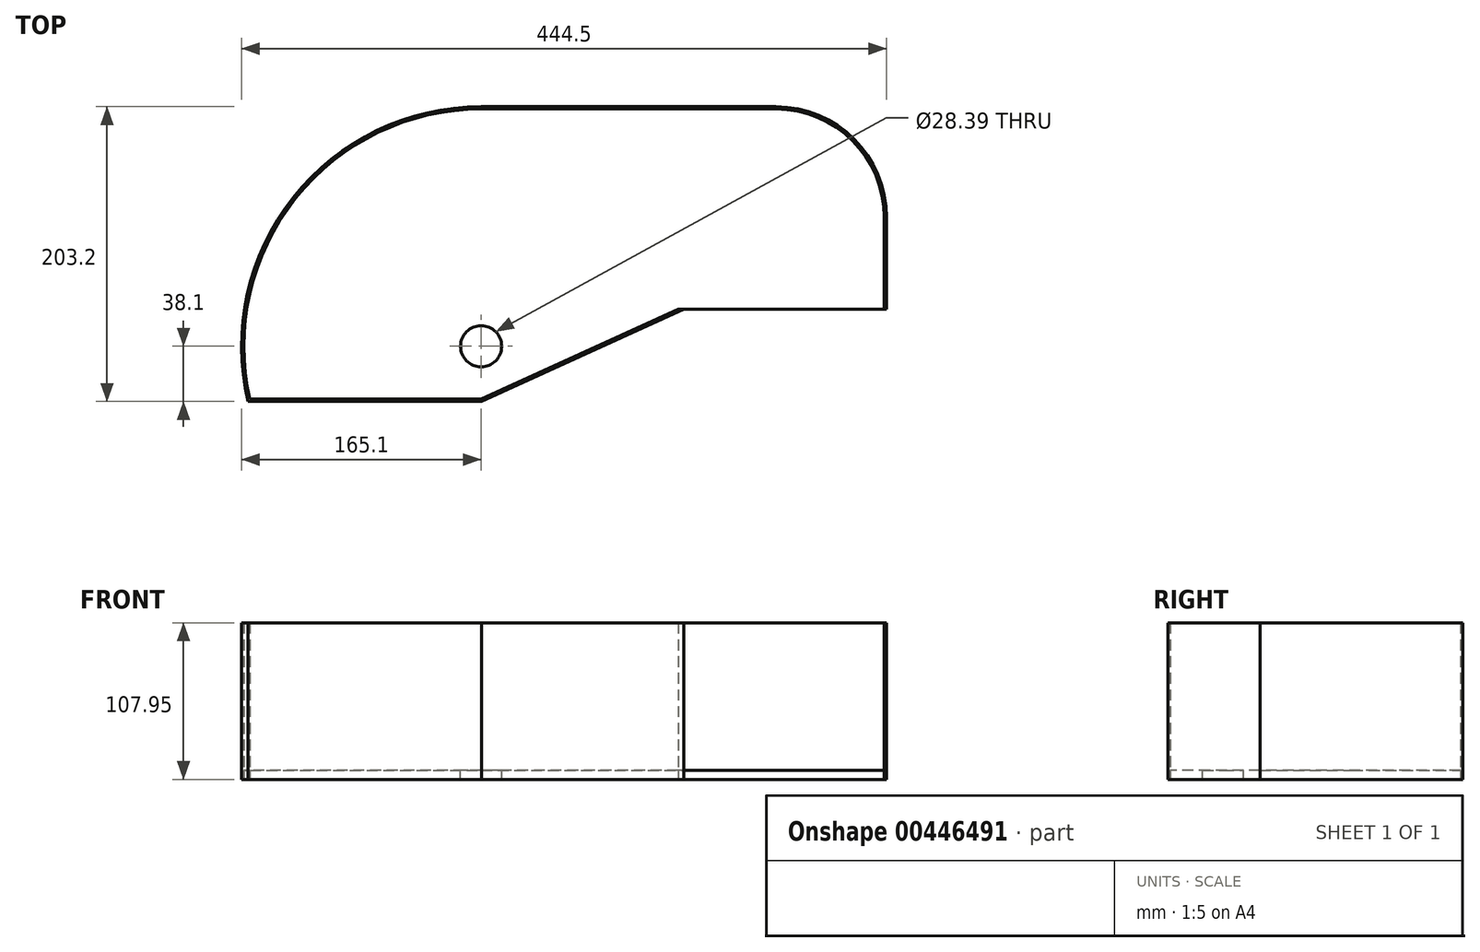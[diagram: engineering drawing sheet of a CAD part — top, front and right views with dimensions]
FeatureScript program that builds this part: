
annotation { "Feature Type Name" : "Feature", "Feature Type Description" : "" }
export const myFeature = defineFeature(function(context is Context, id is Id, definition is map)
    precondition{}
    {
        {
            var Q0;
            Q0=qCreatedBy(makeId("Top.planeOp"),FACE);
            var sketch = newSketch(context, id + "F0", { "sketchPlane" : qUnion([Q0])});
            skLineSegment(sketch, "E0", {"start": v(0, 165.1) * mm, "end": v(203.2, 165.1) * mm});
            skLineSegment(sketch, "E1", {"start": v(279.4, 88.9) * mm, "end": v(279.4, 25.4) * mm});
            skLineSegment(sketch, "E2", {"start": v(279.4, 25.4) * mm, "end": v(139.7, 25.4) * mm});
            skLineSegment(sketch, "E3", {"start": v(-160.64, -38.1) * mm, "end": v(0.34, -38.1) * mm});
            skPoint(sketch, "E4.end.orphan", {"position": v(0.34, -38.1) * mm});
            skArc(sketch, "E5.trimOffspring", {"start": v(0, 165.1) * mm, "mid": v(-129.52, 102.4) * mm, "end": v(-160.64, -38.1) * mm});
            skPoint(sketch, "E6.visualSharp", {"position": v(279.4, 165.1) * mm});
            skArc(sketch, "E6.filletArc", {"start": v(279.4, 88.9) * mm, "mid": v(257.08, 142.78) * mm, "end": v(203.2, 165.1) * mm});
            skLineSegment(sketch, "E7", {"start": v(139.7, 25.4) * mm, "end": v(0.34, -38.1) * mm});
            skArc(sketch, "E8.0", {"start": v(0, 163.51) * mm, "mid": v(-127.88, 101.9) * mm, "end": v(-159.38, -36.51) * mm});
            skLineSegment(sketch, "E8.1", {"start": v(-159.38, -36.51) * mm, "end": v(0, -36.51) * mm});
            skArc(sketch, "E8.2", {"start": v(277.81, 88.9) * mm, "mid": v(255.96, 141.66) * mm, "end": v(203.2, 163.51) * mm});
            skLineSegment(sketch, "E8.3", {"start": v(277.81, 88.9) * mm, "end": v(277.81, 26.99) * mm});
            skLineSegment(sketch, "E8.5", {"start": v(0, 163.51) * mm, "end": v(203.2, 163.51) * mm});
            skLineSegment(sketch, "E8.6", {"start": v(135.87, 25.4) * mm, "end": v(0, -36.51) * mm});
            skLineSegment(sketch, "E9", {"start": v(139.7, 25.4) * mm, "end": v(135.87, 25.4) * mm});
            skLineSegment(sketch, "E10", {"start": v(277.81, 25.4) * mm, "end": v(277.81, 26.99) * mm});
            skSolve(sketch);
        }
        {
            var Q0;
            Q0=makeQuery(id+"F0.imprint","IMPRINT",FACE,{"disambiguationData":[TD([[makeQuery(id+"F0.imprint","IMPRINT",EDGE,{"derivedFrom":sQuery(id+"F0.wireOp",EDGE,"E0")}),-1.0]])]});
            extrude(context, id + "F1", {"entities" : qUnion([Q0]), "depth" : 107.95 * mm});
        }
        {
            var Q0;
            Q0=makeQuery(id+"F0.imprint","IMPRINT",FACE,{"disambiguationData":[TD([[makeQuery(id+"F0.imprint","IMPRINT",EDGE,{"derivedFrom":sQuery(id+"F0.wireOp",EDGE,"E8.0")}),1.0]])]});
            extrude(context, id + "F2", {"entities" : qUnion([Q0]), "depth" : 6.35 * mm});
        }
        {
            var Q0;
            Q0=makeQuery(id+"F2.opExtrude","CAP_FACE",FACE,{"disambiguationData":[OSD([sQuery(id+"F0.wireOp",EDGE,"E2"),sQuery(id+"F0.wireOp",EDGE,"E8.0"),sQuery(id+"F0.wireOp",EDGE,"E8.1"),sQuery(id+"F0.wireOp",EDGE,"E8.2"),sQuery(id+"F0.wireOp",EDGE,"E8.3"),sQuery(id+"F0.wireOp",EDGE,"E8.5"),sQuery(id+"F0.wireOp",EDGE,"E8.6"),sQuery(id+"F0.wireOp",EDGE,"E9"),sQuery(id+"F0.wireOp",EDGE,"E10")])],"isStart":false});
            var sketch = newSketch(context, id + "F3", { "sketchPlane" : qUnion([Q0])});
            skCircle(sketch, "E11", {"center": v(0, 0) * mm, "radius": 14.2 * mm});
            skSolve(sketch);
        }
        {
            var Q0;
            Q0=makeQuery(id+"F3.imprint","IMPRINT",FACE,{"disambiguationData":[TD([[makeQuery(id+"F3.imprint","IMPRINT",EDGE,{"derivedFrom":sQuery(id+"F3.wireOp",EDGE,"E11")}),1.0]])]});
            extrude(context, id + "F4", {"entities" : qUnion([Q0]), "operationType" : NewBodyOperationType.REMOVE, "oppositeDirection" : true, "depth" : 6.35 * mm});
        }
    });
